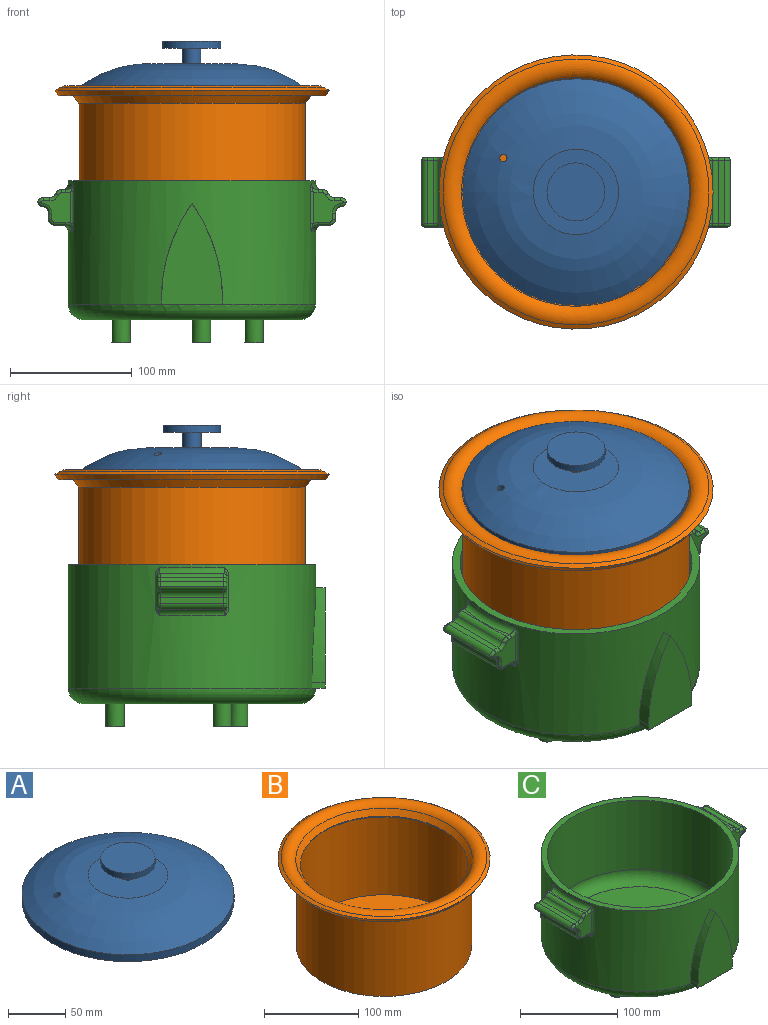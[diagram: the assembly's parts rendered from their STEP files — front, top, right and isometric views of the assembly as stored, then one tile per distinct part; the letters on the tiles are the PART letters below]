
ASSEMBLY  parts=3 mates=2
PART A: 12 faces, bbox 185.9x185.9x45.8 mm
  f0: torus R=35.05mm, axis (0,0,-1), area 19968.1mm2, adj f2,f3,f11
  f1: torus R=35.05mm, axis (0,0,-1), area 25482.5mm2, adj f5,f6,f11
  f2: plane 88.12x88.12mm, normal (0,0,-1), area 6099.1mm2, adj f0
  f3: cylinder r=87.88mm len=175.77mm, axis (0,0,-1), area 1609.2mm2, adj f0,f4
  f4: plane 185.93x185.93mm, normal (0,0,-1), area 2886.2mm2, adj f3,f5
  f5: cylinder r=92.96mm len=185.93mm, axis (0,0,-1), area 4287.7mm2, adj f1,f4
  f6: plane 70.1x70.1mm, normal (0,0,1), area 3677.5mm2, adj f1,f7
  f7: cylinder r=7.62mm len=15.24mm, axis (0,0,-1), area 608mm2, adj f6,f8
  f8: plane 47.63x47.63mm, normal (0,0,-1), area 1599mm2, adj f7,f9
  f9: cylinder r=23.81mm len=47.63mm, axis (0,0,-1), area 874.1mm2, adj f8,f10
  f10: plane 47.63x47.63mm, normal (0,0,1), area 1781.4mm2, adj f9
  f11: cylinder r=3.05mm len=9.22mm, axis (0,0,-1), area 134.5mm2, adj f0,f1
PART B: 13 faces, bbox 240.6x240.6x117.2 mm
  f0: torus R=103.03mm, axis (0,0,1), area 6073.3mm2, adj f1,f8
  f1: cone r=106.4mm half-angle=58deg, axis (0,0,-1), area 2788.7mm2, adj f0,f2
  f2: cone r=109.88mm half-angle=32deg, axis (0,0,1), area 3550.2mm2, adj f1,f3
  f3: cone r=109.1mm half-angle=58deg, axis (0,0,-1), area 2858.2mm2, adj f2,f4
  f4: torus R=103.03mm, axis (0,0,1), area 10839.7mm2, adj f3,f5
  f5: cone r=88.88mm half-angle=36.5deg, axis (0,0,1), area 4790.5mm2, adj f4,f9
  f6: plane 185.93x185.93mm, normal (0,0,-1), area 27150.6mm2, adj f7
  f7: cylinder r=92.96mm len=185.93mm, axis (0,0,1), area 60087.4mm2, adj f6,f8
  f8: cone r=92.96mm half-angle=36.5deg, axis (0,0,1), area 5004.6mm2, adj f0,f7
  f9: cone r=88.88mm half-angle=88.1deg, axis (0,0,1), area 1844.2mm2, adj f5,f12
  f10: plane 180.85x180.85mm, normal (0,0,1), area 25687.2mm2, adj f11
  f11: cylinder r=90.42mm len=180.85mm, axis (0,0,1), area 57478.4mm2, adj f10,f12
  f12: cone r=90.92mm half-angle=36.5deg, axis (0,0,1), area 1636.9mm2, adj f9,f11
PART C: 111 faces, bbox 254.5x219.9x134.4 mm
  f0: cylinder r=101.6mm len=203.2mm, axis (0,0,-1), area 57189.5mm2, adj f1,f10,f33,f34,f35,f36,f53,f55
  f1: plane 203.2x203.2mm, normal (0,0,1), area 3927mm2, adj f0,f2
  f2: cylinder r=95.25mm len=190.5mm, axis (0,0,-1), area 52097.2mm2, adj f1,f3
  f3: torus R=82.55mm, axis (0,0,-1), area 11360.6mm2, adj f2,f4
  f4: plane 165.1x165.1mm, normal (0,0,1), area 20111.2mm2, adj f3,f5
  f5: cylinder r=20.32mm len=40.64mm, axis (0,0,-1), area 825.6mm2, adj f4,f6
  f6: plane 40.64x40.64mm, normal (0,0,1), area 373.7mm2, adj f5,f7
  f7: cylinder r=17.14mm len=34.29mm, axis (0,0,-1), area 1607.6mm2, adj f6,f8
  f8: plane 34.29x34.29mm, normal (0,0,1), area 923.5mm2, adj f7
  f9: plane 177.8x177.8mm, normal (0,0,-1), area 24281.4mm2, adj f10,f11,f13,f15
  f10: torus R=88.9mm, axis (0,0,-1), area 12156.5mm2, adj f0,f9,f109
  f11: cylinder r=7.62mm len=19.05mm, axis (0,0,1), area 912.1mm2, adj f9,f12
  f12: plane 15.24x15.24mm, normal (0,0,-1), area 182.4mm2, adj f11
  f13: cylinder r=7.62mm len=19.05mm, axis (0,0,1), area 912.1mm2, adj f9,f14
  f14: plane 15.24x15.24mm, normal (0,0,-1), area 182.4mm2, adj f13
  f15: cylinder r=7.62mm len=19.05mm, axis (0,0,1), area 912.1mm2, adj f9,f16
  f16: plane 15.24x15.24mm, normal (0,0,-1), area 182.4mm2, adj f15
  f17: plane 26.34x24.76mm, normal (0,1,0), area 390.9mm2, adj f60,f61,f62,f63,f64,f65,f66,f67
  f18: plane 26.34x24.76mm, normal (0,-1,0), area 390.9mm2, adj f45,f46,f47,f48,f49,f50,f51,f52
  f19: plane 52.07x3.77mm, normal (0,0,1), area 83.9mm2, adj f35,f44,f49,f65
  f20: plane 52.07x9.31mm, normal (0,0,-1), area 372.5mm2, adj f36,f41,f58,f72
  f21: plane 52.07x5.08mm, normal (1,0,0), area 264.5mm2, adj f31,f41,f54,f68
  f22: plane 52.07x5.28mm, normal (0,0,1), area 274.8mm2, adj f32,f42,f46,f60
  f23: plane 26.34x24.76mm, normal (0,1,0), area 390.9mm2, adj f75,f76,f77,f78,f79,f80,f81,f82
  f24: plane 26.34x24.76mm, normal (0,-1,0), area 390.9mm2, adj f90,f91,f92,f93,f94,f95,f96,f97
  f25: plane 52.07x5.08mm, normal (-1,0,0), area 264.5mm2, adj f29,f37,f76,f90
  f26: plane 52.07x9.31mm, normal (0,0,-1), area 372.5mm2, adj f33,f37,f80,f94
  f27: plane 52.07x3.77mm, normal (0,0,1), area 83.9mm2, adj f34,f38,f87,f103
  f28: plane 52.07x5.28mm, normal (0,0,1), area 274.8mm2, adj f30,f40,f81,f97
  f29: cylinder r=5.08mm len=52.07mm, axis (0,1,0), area 389.3mm2, adj f25,f39,f75,f91
  f30: cylinder r=5.08mm len=52.07mm, axis (0,1,0), area 313.8mm2, adj f28,f38,f83,f99
  f31: cylinder r=5.08mm len=52.07mm, axis (0,1,0), area 389.3mm2, adj f21,f43,f52,f66
  f32: cylinder r=5.08mm len=52.07mm, axis (0,1,0), area 313.8mm2, adj f22,f44,f45,f61
  f33: torus R=106.68mm, axis (0,0,-1), area 422.9mm2, adj f0,f26,f82,f96
  f34: torus R=106.68mm, axis (0,0,1), area 422.9mm2, adj f0,f27,f89,f104
  f35: torus R=106.68mm, axis (0,0,-1), area 422.9mm2, adj f0,f19,f51,f67
  f36: torus R=106.68mm, axis (0,0,1), area 422.9mm2, adj f0,f20,f59,f74
  f37: cylinder r=5.08mm len=52.07mm, axis (0,-1,0), area 415.5mm2, adj f25,f26,f78,f92
  f38: cylinder r=5.08mm len=52.07mm, axis (0,1,0), area 313.8mm2, adj f27,f30,f85,f101
  f39: cylinder r=5.08mm len=52.07mm, axis (0,1,0), area 323.8mm2, adj f29,f40,f77,f93
  f40: cylinder r=5.08mm len=52.07mm, axis (0,-1,0), area 350mm2, adj f28,f39,f79,f95
  f41: cylinder r=5.08mm len=52.07mm, axis (0,-1,0), area 415.5mm2, adj f20,f21,f56,f70
  f42: cylinder r=5.08mm len=52.07mm, axis (0,-1,0), area 350mm2, adj f22,f43,f48,f62
  f43: cylinder r=5.08mm len=52.07mm, axis (0,1,0), area 323.8mm2, adj f31,f42,f50,f64
  f44: cylinder r=5.08mm len=52.07mm, axis (0,1,0), area 313.8mm2, adj f19,f32,f47,f63
  f45: torus R=7.62mm, axis (0,-1,0), area 28.4mm2, adj f18,f32,f46,f47
  f46: cylinder r=2.54mm len=5.28mm, axis (-1,0,0), area 21.1mm2, adj f18,f22,f45,f48
  f47: torus R=2.54mm, axis (0,-1,0), area 19.7mm2, adj f18,f44,f45,f49
  f48: torus R=2.54mm, axis (0,-1,0), area 20mm2, adj f18,f42,f46,f50
  f49: cylinder r=2.54mm len=3.77mm, axis (-1,0,0), area 15mm2, adj f18,f19,f47,f51
  f50: torus R=2.54mm, axis (0,-1,0), area 18.3mm2, adj f18,f43,f48,f52
  f51: bspline ~9.67x9.12mm, area 23.5mm2, adj f18,f35,f49,f53
  f52: torus R=7.62mm, axis (0,-1,0), area 35.2mm2, adj f18,f31,f50,f54
  f53: bspline ~6.52x3.65mm, area 8.4mm2, adj f0,f51,f55
  f54: cylinder r=2.54mm len=5.08mm, axis (0,0,1), area 20.3mm2, adj f18,f21,f52,f56
  f55: cylinder r=2.54mm len=26.33mm, axis (0,0,-1), area 84.8mm2, adj f0,f18,f53,f57
  f56: torus R=2.54mm, axis (0,-1,0), area 26.1mm2, adj f18,f41,f54,f58
  f57: bspline ~6.52x3.65mm, area 7.7mm2, adj f0,f55,f59
  f58: cylinder r=2.54mm len=9.31mm, axis (1,0,0), area 37.1mm2, adj f18,f20,f56,f59
  f59: bspline ~9.67x9.12mm, area 23.5mm2, adj f18,f36,f57,f58
  f60: cylinder r=2.54mm len=5.28mm, axis (1,0,0), area 21.1mm2, adj f17,f22,f61,f62
  f61: torus R=7.62mm, axis (0,-1,0), area 28.4mm2, adj f17,f32,f60,f63
  f62: torus R=2.54mm, axis (0,-1,0), area 20mm2, adj f17,f42,f60,f64
  f63: torus R=2.54mm, axis (0,-1,0), area 19.7mm2, adj f17,f44,f61,f65
  f64: torus R=2.54mm, axis (0,-1,0), area 18.3mm2, adj f17,f43,f62,f66
  f65: cylinder r=2.54mm len=3.77mm, axis (1,0,0), area 15mm2, adj f17,f19,f63,f67
  f66: torus R=7.62mm, axis (0,-1,0), area 35.2mm2, adj f17,f31,f64,f68
  f67: bspline ~9.67x9.12mm, area 23.5mm2, adj f17,f35,f65,f69
  f68: cylinder r=2.54mm len=5.08mm, axis (0,0,-1), area 20.3mm2, adj f17,f21,f66,f70
  f69: bspline ~6.52x3.65mm, area 7.7mm2, adj f0,f67,f71
  f70: torus R=2.54mm, axis (0,-1,0), area 26.1mm2, adj f17,f41,f68,f72
  f71: cylinder r=2.54mm len=26.33mm, axis (0,0,-1), area 84.8mm2, adj f0,f17,f69,f73
  f72: cylinder r=2.54mm len=9.31mm, axis (-1,0,0), area 37.1mm2, adj f17,f20,f70,f74
  f73: bspline ~6.52x3.65mm, area 8.4mm2, adj f0,f71,f74
  f74: bspline ~9.67x9.12mm, area 23.5mm2, adj f17,f36,f72,f73
  f75: torus R=7.62mm, axis (0,-1,0), area 35.2mm2, adj f23,f29,f76,f77
  f76: cylinder r=2.54mm len=5.08mm, axis (0,0,1), area 20.3mm2, adj f23,f25,f75,f78
  f77: torus R=2.54mm, axis (0,-1,0), area 18.3mm2, adj f23,f39,f75,f79
  f78: torus R=2.54mm, axis (0,-1,0), area 26.1mm2, adj f23,f37,f76,f80
  f79: torus R=2.54mm, axis (0,-1,0), area 20mm2, adj f23,f40,f77,f81
  f80: cylinder r=2.54mm len=9.31mm, axis (-1,0,0), area 37.1mm2, adj f23,f26,f78,f82
  f81: cylinder r=2.54mm len=5.28mm, axis (1,0,0), area 21.1mm2, adj f23,f28,f79,f83
  f82: bspline ~9.67x9.12mm, area 23.5mm2, adj f23,f33,f80,f84
  f83: torus R=7.62mm, axis (0,-1,0), area 28.4mm2, adj f23,f30,f81,f85
  f84: bspline ~6.52x3.65mm, area 7.7mm2, adj f0,f82,f86
  f85: torus R=2.54mm, axis (0,-1,0), area 19.7mm2, adj f23,f38,f83,f87
  f86: cylinder r=2.54mm len=26.33mm, axis (0,0,-1), area 84.8mm2, adj f0,f23,f84,f88
  f87: cylinder r=2.54mm len=3.77mm, axis (1,0,0), area 15mm2, adj f23,f27,f85,f89
  f88: bspline ~6.52x3.65mm, area 8.4mm2, adj f0,f86,f89
  f89: bspline ~9.67x9.12mm, area 23.5mm2, adj f23,f34,f87,f88
  f90: cylinder r=2.54mm len=5.08mm, axis (0,0,-1), area 20.3mm2, adj f24,f25,f91,f92
  f91: torus R=7.62mm, axis (0,-1,0), area 35.2mm2, adj f24,f29,f90,f93
  f92: torus R=2.54mm, axis (0,-1,0), area 26.1mm2, adj f24,f37,f90,f94
  f93: torus R=2.54mm, axis (0,-1,0), area 18.3mm2, adj f24,f39,f91,f95
  f94: cylinder r=2.54mm len=9.31mm, axis (1,0,0), area 37.1mm2, adj f24,f26,f92,f96
  f95: torus R=2.54mm, axis (0,-1,0), area 20mm2, adj f24,f40,f93,f97
  f96: bspline ~9.67x9.12mm, area 23.5mm2, adj f24,f33,f94,f98
  f97: cylinder r=2.54mm len=5.28mm, axis (-1,0,0), area 21.1mm2, adj f24,f28,f95,f99
  f98: bspline ~6.52x3.65mm, area 8.4mm2, adj f0,f96,f100
  f99: torus R=7.62mm, axis (0,-1,0), area 28.4mm2, adj f24,f30,f97,f101
  f100: cylinder r=2.54mm len=26.33mm, axis (0,0,-1), area 84.8mm2, adj f0,f24,f98,f102
  f101: torus R=2.54mm, axis (0,-1,0), area 19.7mm2, adj f24,f38,f99,f103
  f102: bspline ~6.52x3.65mm, area 7.7mm2, adj f0,f100,f104
  f103: cylinder r=2.54mm len=3.77mm, axis (-1,0,0), area 15mm2, adj f24,f27,f101,f104
  f104: bspline ~9.67x9.12mm, area 23.5mm2, adj f24,f34,f102,f103
  f105: cylinder r=133.37mm len=77.85mm, axis (0,1,0), area 764.1mm2, adj f0,f106,f108,f110
  f106: cylinder r=133.37mm len=77.85mm, axis (0,1,0), area 764.1mm2, adj f0,f105,f107,f110
  f107: plane 10.76x4.7mm, normal (-1,0,0), area 50.6mm2, adj f0,f106,f109,f110
  f108: plane 10.76x4.7mm, normal (1,0,0), area 50.6mm2, adj f0,f105,f109,f110
  f109: plane 50.15x10.76mm, normal (0,0,-1), area 434.4mm2, adj f10,f107,f108,f110
  f110: plane 82.55x50.15mm, normal (0,-1,0), area 2892mm2, adj f105,f106,f107,f108,f109
PLACE A t=(332.06,134.02,256.11)mm
PLACE B t=(331.2,134.02,250.83)mm
PLACE C t=(331.2,134.02,73.05)mm
MATE slider B.f0 <-> C.f0  axis (0,0,1) through (331.2,134.02,201.08)mm
MATE fastened B.f0 <-> A.f3  axis (0,0,1) through (331.2,134.02,263.45)mm
